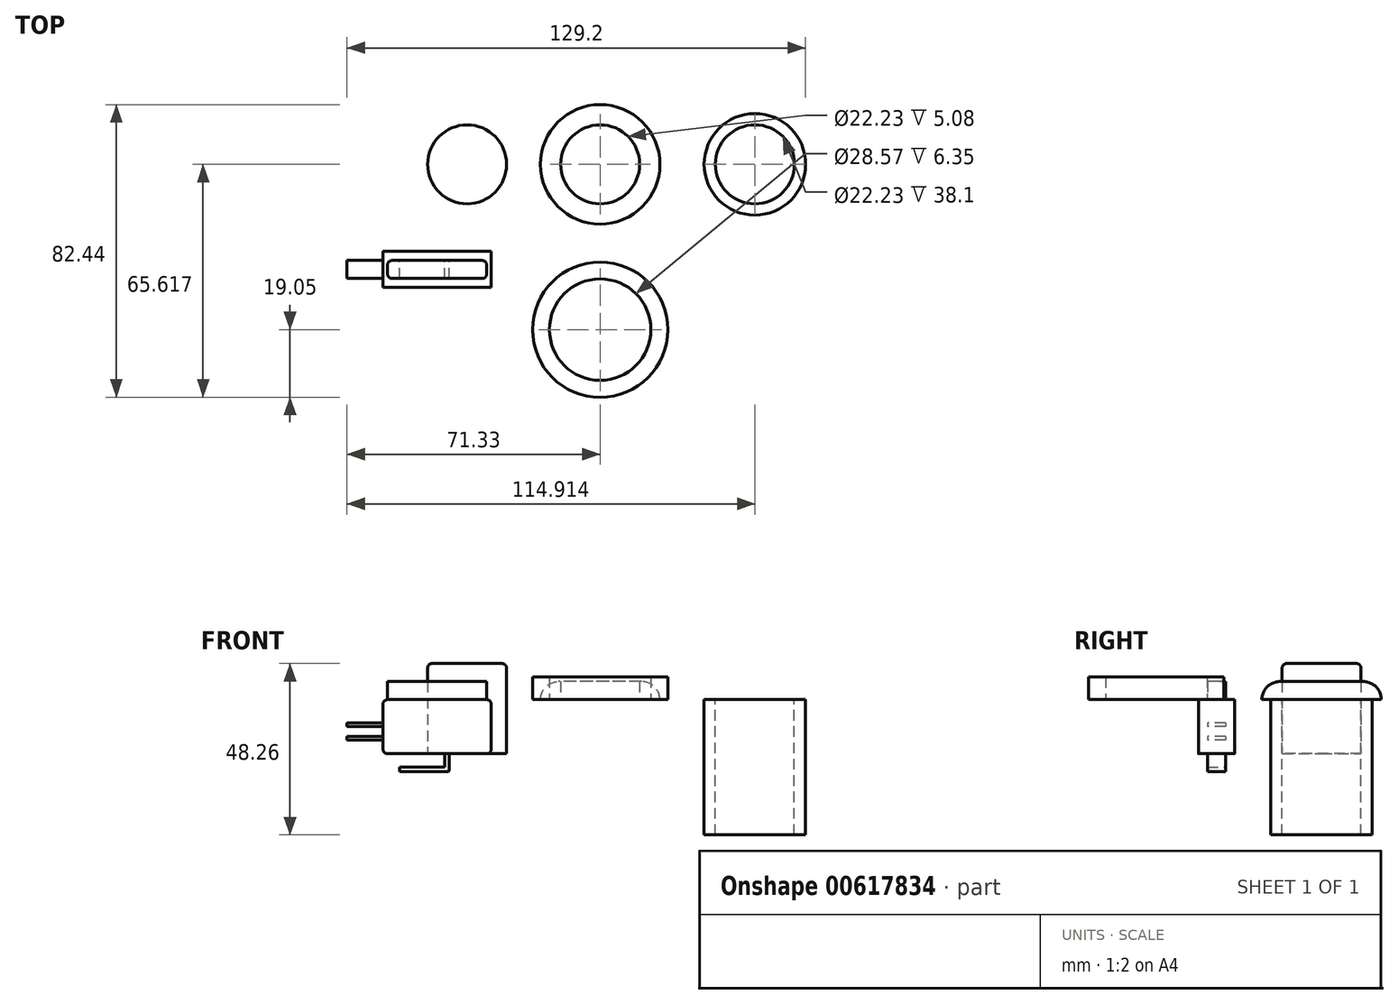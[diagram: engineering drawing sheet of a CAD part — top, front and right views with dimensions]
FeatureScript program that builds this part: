
annotation { "Feature Type Name" : "Feature", "Feature Type Description" : "" }
export const myFeature = defineFeature(function(context is Context, id is Id, definition is map)
    precondition{}
    {
        {
            var Q0;
            Q0=qCreatedBy(makeId("Top.planeOp"),FACE);
            var sketch = newSketch(context, id + "F0", { "sketchPlane" : qUnion([Q0])});
            skLineSegment(sketch, "E0.bottom", {"start": v(-30.69, 22.03) * mm, "end": v(-61.17, 22.03) * mm});
            skLineSegment(sketch, "E0.top", {"start": v(-30.69, 11.87) * mm, "end": v(-61.17, 11.87) * mm});
            skLineSegment(sketch, "E0.left", {"start": v(-30.69, 22.03) * mm, "end": v(-30.69, 11.87) * mm});
            skLineSegment(sketch, "E0.right", {"start": v(-61.17, 22.03) * mm, "end": v(-61.17, 11.87) * mm});
            skPoint(sketch, "E0.middle", {"position": v(-45.93, 16.95) * mm});
            skSolve(sketch);
        }
        {
            var Q0;
            Q0=makeQuery(id+"F0.imprint","IMPRINT",FACE,{"disambiguationData":[TD([[makeQuery(id+"F0.imprint","IMPRINT",EDGE,{"derivedFrom":sQuery(id+"F0.wireOp",EDGE,"E0.bottom")}),1.0]])]});
            extrude(context, id + "F1", {"entities" : qUnion([Q0]), "oppositeDirection" : true, "depth" : 15.24 * mm, "offsetDistance" : 25.4 * mm});
        }
        {
            var Q0;
            Q0=makeQuery(id+"F1.opExtrude","SWEPT_FACE",FACE,{"disambiguationData":[OSD([sQuery(id+"F0.wireOp",EDGE,"E0.right")])]});
            var sketch = newSketch(context, id + "F2", { "sketchPlane" : qUnion([Q0])});
            skLineSegment(sketch, "E1", {"start": v(-22.03, -6.6) * mm, "end": v(-19.49, -6.6) * mm, "construction": true});
            skLineSegment(sketch, "E2", {"start": v(-11.87, -6.6) * mm, "end": v(-14.4, -6.6) * mm, "construction": true});
            skLineSegment(sketch, "E3.bottom", {"start": v(-19.49, -6.6) * mm, "end": v(-14.4, -6.6) * mm});
            skLineSegment(sketch, "E3.top", {"start": v(-19.49, -7.62) * mm, "end": v(-14.4, -7.62) * mm});
            skLineSegment(sketch, "E3.left", {"start": v(-19.49, -6.6) * mm, "end": v(-19.49, -7.62) * mm});
            skLineSegment(sketch, "E3.right", {"start": v(-14.4, -6.6) * mm, "end": v(-14.4, -7.62) * mm});
            skLineSegment(sketch, "E4.bottom", {"start": v(-19.49, -10.41) * mm, "end": v(-14.4, -10.41) * mm});
            skLineSegment(sketch, "E4.top", {"start": v(-19.49, -11.43) * mm, "end": v(-14.4, -11.43) * mm});
            skLineSegment(sketch, "E4.left", {"start": v(-19.49, -10.41) * mm, "end": v(-19.49, -11.43) * mm});
            skLineSegment(sketch, "E4.right", {"start": v(-14.4, -10.41) * mm, "end": v(-14.4, -11.43) * mm});
            skSolve(sketch);
        }
        {
            var Q0;
            Q0=makeQuery(id+"F2.imprint","IMPRINT",FACE,{"disambiguationData":[TD([[makeQuery(id+"F2.imprint","IMPRINT",EDGE,{"derivedFrom":sQuery(id+"F2.wireOp",EDGE,"E3.bottom")}),-1.0]])]});
            var Q1;
            Q1=makeQuery(id+"F2.imprint","IMPRINT",FACE,{"disambiguationData":[TD([[makeQuery(id+"F2.imprint","IMPRINT",EDGE,{"derivedFrom":sQuery(id+"F2.wireOp",EDGE,"E4.bottom")}),-1.0]])]});
            extrude(context, id + "F3", {"entities" : qUnion([Q0, Q1]), "operationType" : NewBodyOperationType.ADD, "depth" : 10.16 * mm, "offsetDistance" : 25.4 * mm});
        }
        {
            var Q0;
            Q0=makeQuery(id+"F1.opExtrude","CAP_FACE",FACE,{"disambiguationData":[OSD([sQuery(id+"F0.wireOp",EDGE,"E0.bottom"),sQuery(id+"F0.wireOp",EDGE,"E0.top"),sQuery(id+"F0.wireOp",EDGE,"E0.left"),sQuery(id+"F0.wireOp",EDGE,"E0.right")])],"isStart":false});
            var sketch = newSketch(context, id + "F4", { "sketchPlane" : qUnion([Q0])});
            skLineSegment(sketch, "E5.bottom", {"start": v(-43.77, -14.4) * mm, "end": v(-42.5, -14.4) * mm});
            skLineSegment(sketch, "E5.top", {"start": v(-43.77, -19.49) * mm, "end": v(-42.5, -19.49) * mm});
            skLineSegment(sketch, "E5.left", {"start": v(-43.77, -14.4) * mm, "end": v(-43.77, -19.49) * mm});
            skLineSegment(sketch, "E5.right", {"start": v(-42.5, -14.4) * mm, "end": v(-42.5, -19.49) * mm});
            skLineSegment(sketch, "E6", {"start": v(-42.5, -14.4) * mm, "end": v(-42.5, -11.87) * mm, "construction": true});
            skLineSegment(sketch, "E7", {"start": v(-42.5, -19.49) * mm, "end": v(-42.5, -22.03) * mm, "construction": true});
            skSolve(sketch);
        }
        {
            var Q0;
            Q0=makeQuery(id+"F4.imprint","IMPRINT",FACE,{"disambiguationData":[TD([[makeQuery(id+"F4.imprint","IMPRINT",EDGE,{"derivedFrom":sQuery(id+"F4.wireOp",EDGE,"E5.bottom")}),-1.0]])]});
            extrude(context, id + "F5", {"entities" : qUnion([Q0]), "operationType" : NewBodyOperationType.ADD, "depth" : 5.08 * mm, "offsetDistance" : 25.4 * mm});
        }
        {
            var Q0;
            Q0=makeQuery(id+"F5.opExtrude","SWEPT_FACE",FACE,{"disambiguationData":[OSD([sQuery(id+"F4.wireOp",EDGE,"E5.left")])]});
            var sketch = newSketch(context, id + "F6", { "sketchPlane" : qUnion([Q0])});
            skLineSegment(sketch, "E8.bottom", {"start": v(-14.4, -20.32) * mm, "end": v(-19.49, -20.32) * mm});
            skLineSegment(sketch, "E8.top", {"start": v(-14.4, -19.05) * mm, "end": v(-19.49, -19.05) * mm});
            skLineSegment(sketch, "E8.left", {"start": v(-14.4, -20.32) * mm, "end": v(-14.4, -19.05) * mm});
            skLineSegment(sketch, "E8.right", {"start": v(-19.49, -20.32) * mm, "end": v(-19.49, -19.05) * mm});
            skSolve(sketch);
        }
        {
            var Q0;
            Q0=makeQuery(id+"F6.imprint","IMPRINT",FACE,{"disambiguationData":[TD([[makeQuery(id+"F6.imprint","IMPRINT",EDGE,{"derivedFrom":sQuery(id+"F6.wireOp",EDGE,"E8.bottom")}),-1.0]])]});
            extrude(context, id + "F7", {"entities" : qUnion([Q0]), "operationType" : NewBodyOperationType.ADD, "depth" : 12.7 * mm, "offsetDistance" : 25.4 * mm});
        }
        {
            var Q0;
            Q0=makeQuery(id+"F5.opExtrude","CAP_EDGE",EDGE,{"disambiguationData":[OSD([sQuery(id+"F4.wireOp",EDGE,"E5.right")])],"isStart":false});
            var Q1;
            Q1=makeQuery(id+"F7.opExtrude","CAP_EDGE",EDGE,{"disambiguationData":[OSD([sQuery(id+"F6.wireOp",EDGE,"E8.top")])],"isStart":true});
            fillet(context, id + "F8", {"entities" : qUnion([Q0, Q1]), "radius" : 0.5 * mm, "tangentPropagation" : true, "allowEdgeOverflow" : false});
        }
        {
            var Q0;
            Q0=makeQuery(id+"F1.opExtrude","CAP_EDGE",EDGE,{"disambiguationData":[OSD([sQuery(id+"F0.wireOp",EDGE,"E0.left")])],"isStart":false});
            var Q1;
            Q1=makeQuery(id+"F1.opExtrude","CAP_EDGE",EDGE,{"disambiguationData":[OSD([sQuery(id+"F0.wireOp",EDGE,"E0.right")])],"isStart":false});
            var Q2;
            Q2=makeQuery(id+"F1.opExtrude","CAP_EDGE",EDGE,{"disambiguationData":[OSD([sQuery(id+"F0.wireOp",EDGE,"E0.left")])],"isStart":true});
            var Q3;
            Q3=makeQuery(id+"F1.opExtrude","CAP_EDGE",EDGE,{"disambiguationData":[OSD([sQuery(id+"F0.wireOp",EDGE,"E0.right")])],"isStart":true});
            fillet(context, id + "F9", {"entities" : qUnion([Q0, Q1, Q2, Q3]), "radius" : 1.27 * mm, "tangentPropagation" : true, "allowEdgeOverflow" : false});
        }
        {
            var Q0;
            Q0=makeQuery(id+"F1.opExtrude","CAP_FACE",FACE,{"disambiguationData":[OSD([sQuery(id+"F0.wireOp",EDGE,"E0.bottom"),sQuery(id+"F0.wireOp",EDGE,"E0.top"),sQuery(id+"F0.wireOp",EDGE,"E0.left"),sQuery(id+"F0.wireOp",EDGE,"E0.right")])],"isStart":true});
            var sketch = newSketch(context, id + "F10", { "sketchPlane" : qUnion([Q0])});
            skLineSegment(sketch, "E9.bottom", {"start": v(-59.9, 19.49) * mm, "end": v(-31.96, 19.49) * mm});
            skLineSegment(sketch, "E9.top", {"start": v(-59.9, 14.4) * mm, "end": v(-31.96, 14.4) * mm});
            skLineSegment(sketch, "E9.left", {"start": v(-59.9, 19.49) * mm, "end": v(-59.9, 14.4) * mm});
            skLineSegment(sketch, "E9.right", {"start": v(-31.96, 19.49) * mm, "end": v(-31.96, 14.4) * mm});
            skLineSegment(sketch, "E10", {"start": v(-31.96, 19.49) * mm, "end": v(-31.96, 22.03) * mm, "construction": true});
            skLineSegment(sketch, "E11", {"start": v(-31.96, 14.4) * mm, "end": v(-31.96, 11.87) * mm, "construction": true});
            skSolve(sketch);
        }
        {
            var Q0;
            Q0=makeQuery(id+"F10.imprint","IMPRINT",FACE,{"disambiguationData":[TD([[makeQuery(id+"F10.imprint","IMPRINT",EDGE,{"derivedFrom":sQuery(id+"F10.wireOp",EDGE,"E9.bottom")}),-1.0]])]});
            extrude(context, id + "F11", {"entities" : qUnion([Q0]), "operationType" : NewBodyOperationType.ADD, "depth" : 5.08 * mm, "offsetDistance" : 25.4 * mm});
        }
        {
            var Q0;
            Q0=makeQuery(id+"F11.opExtrude","SWEPT_EDGE",EDGE,{"disambiguationData":[OSD([sQuery(id+"F0.wireOp",EDGE,"E0.bottom"),sQuery(id+"F0.wireOp",EDGE,"E0.top"),sQuery(id+"F0.wireOp",EDGE,"E0.left"),sQuery(id+"F0.wireOp",EDGE,"E0.right"),sQuery(id+"F10.wireOp",EDGE,"E9.top"),sQuery(id+"F10.wireOp",EDGE,"E9.right")])]});
            var Q1;
            Q1=makeQuery(id+"F11.opExtrude","SWEPT_EDGE",EDGE,{"disambiguationData":[OSD([sQuery(id+"F0.wireOp",EDGE,"E0.bottom"),sQuery(id+"F0.wireOp",EDGE,"E0.top"),sQuery(id+"F0.wireOp",EDGE,"E0.left"),sQuery(id+"F0.wireOp",EDGE,"E0.right"),sQuery(id+"F10.wireOp",EDGE,"E9.top"),sQuery(id+"F10.wireOp",EDGE,"E9.left")])]});
            var Q2;
            Q2=makeQuery(id+"F11.opExtrude","SWEPT_EDGE",EDGE,{"disambiguationData":[OSD([sQuery(id+"F0.wireOp",EDGE,"E0.bottom"),sQuery(id+"F0.wireOp",EDGE,"E0.top"),sQuery(id+"F0.wireOp",EDGE,"E0.left"),sQuery(id+"F0.wireOp",EDGE,"E0.right"),sQuery(id+"F10.wireOp",EDGE,"E9.bottom"),sQuery(id+"F10.wireOp",EDGE,"E9.left")])]});
            var Q3;
            Q3=makeQuery(id+"F11.opExtrude","SWEPT_EDGE",EDGE,{"disambiguationData":[OSD([sQuery(id+"F0.wireOp",EDGE,"E0.bottom"),sQuery(id+"F0.wireOp",EDGE,"E0.top"),sQuery(id+"F0.wireOp",EDGE,"E0.left"),sQuery(id+"F0.wireOp",EDGE,"E0.right"),sQuery(id+"F10.wireOp",EDGE,"E9.bottom"),sQuery(id+"F10.wireOp",EDGE,"E9.right")])]});
            fillet(context, id + "F12", {"entities" : qUnion([Q0, Q1, Q2, Q3]), "radius" : 1.27 * mm, "tangentPropagation" : true, "allowEdgeOverflow" : false});
        }
        {
            var Q0;
            Q0=qCreatedBy(makeId("Top.planeOp"),FACE);
            var sketch = newSketch(context, id + "F13", { "sketchPlane" : qUnion([Q0])});
            skCircle(sketch, "E12", {"center": v(0, 46.57) * mm, "radius": 11.11 * mm});
            skCircle(sketch, "E13", {"center": v(0, 46.57) * mm, "radius": 16.83 * mm});
            skCircle(sketch, "E14", {"center": v(43.58, 46.57) * mm, "radius": 11.11 * mm});
            skCircle(sketch, "E15", {"center": v(43.58, 46.57) * mm, "radius": 14.29 * mm});
            skCircle(sketch, "E16", {"center": v(-37.48, 46.57) * mm, "radius": 11.11 * mm});
            skCircle(sketch, "E17", {"center": v(0, 0) * mm, "radius": 19.05 * mm});
            skCircle(sketch, "E18", {"center": v(0, 0) * mm, "radius": 14.29 * mm});
            skSolve(sketch);
        }
        {
            var Q0;
            Q0=makeQuery(id+"F13.imprint","IMPRINT",FACE,{"disambiguationData":[TD([[makeQuery(id+"F13.imprint","IMPRINT",EDGE,{"derivedFrom":sQuery(id+"F13.wireOp",EDGE,"E14")}),-1.0]])]});
            extrude(context, id + "F14", {"entities" : qUnion([Q0]), "oppositeDirection" : true, "depth" : 38.1 * mm, "offsetDistance" : 25.4 * mm});
        }
        {
            var Q0;
            Q0=makeQuery(id+"F13.imprint","IMPRINT",FACE,{"disambiguationData":[TD([[makeQuery(id+"F13.imprint","IMPRINT",EDGE,{"derivedFrom":sQuery(id+"F13.wireOp",EDGE,"E12")}),-1.0]])]});
            extrude(context, id + "F15", {"entities" : qUnion([Q0]), "depth" : 5.08 * mm, "offsetDistance" : 25.4 * mm});
        }
        {
            var Q0;
            Q0=makeQuery(id+"F13.imprint","IMPRINT",FACE,{"disambiguationData":[TD([[makeQuery(id+"F13.imprint","IMPRINT",EDGE,{"derivedFrom":sQuery(id+"F13.wireOp",EDGE,"E16")}),1.0]])]});
            extrude(context, id + "F16", {"entities" : qUnion([Q0]), "depth" : 10.16 * mm, "offsetDistance" : 25.4 * mm});
        }
        {
            var Q0;
            Q0=makeQuery(id+"F16.opExtrude","CAP_FACE",FACE,{"disambiguationData":[OSD([sQuery(id+"F13.wireOp",EDGE,"E16")])],"isStart":true});
            extrude(context, id + "F17", {"entities" : qUnion([Q0]), "operationType" : NewBodyOperationType.ADD, "depth" : 15.24 * mm, "offsetDistance" : 25.4 * mm});
        }
        {
            var Q0;
            Q0=makeQuery(id+"F16.opExtrude","CAP_EDGE",EDGE,{"disambiguationData":[OSD([sQuery(id+"F13.wireOp",EDGE,"E16")])],"isStart":false});
            fillet(context, id + "F18", {"entities" : qUnion([Q0]), "radius" : 1.27 * mm, "tangentPropagation" : true, "allowEdgeOverflow" : false});
        }
        {
            var Q0;
            Q0=makeQuery(id+"F15.opExtrude","CAP_EDGE",EDGE,{"disambiguationData":[OSD([sQuery(id+"F13.wireOp",EDGE,"E13")])],"isStart":false});
            fillet(context, id + "F19", {"entities" : qUnion([Q0]), "radius" : 5.08 * mm, "tangentPropagation" : true, "allowEdgeOverflow" : false});
        }
        {
            var Q0;
            Q0=makeQuery(id+"F13.imprint","IMPRINT",FACE,{"disambiguationData":[TD([[makeQuery(id+"F13.imprint","IMPRINT",EDGE,{"derivedFrom":sQuery(id+"F13.wireOp",EDGE,"E17")}),1.0]])]});
            extrude(context, id + "F20", {"entities" : qUnion([Q0]), "depth" : 6.35 * mm, "offsetDistance" : 25.4 * mm});
        }
    });
